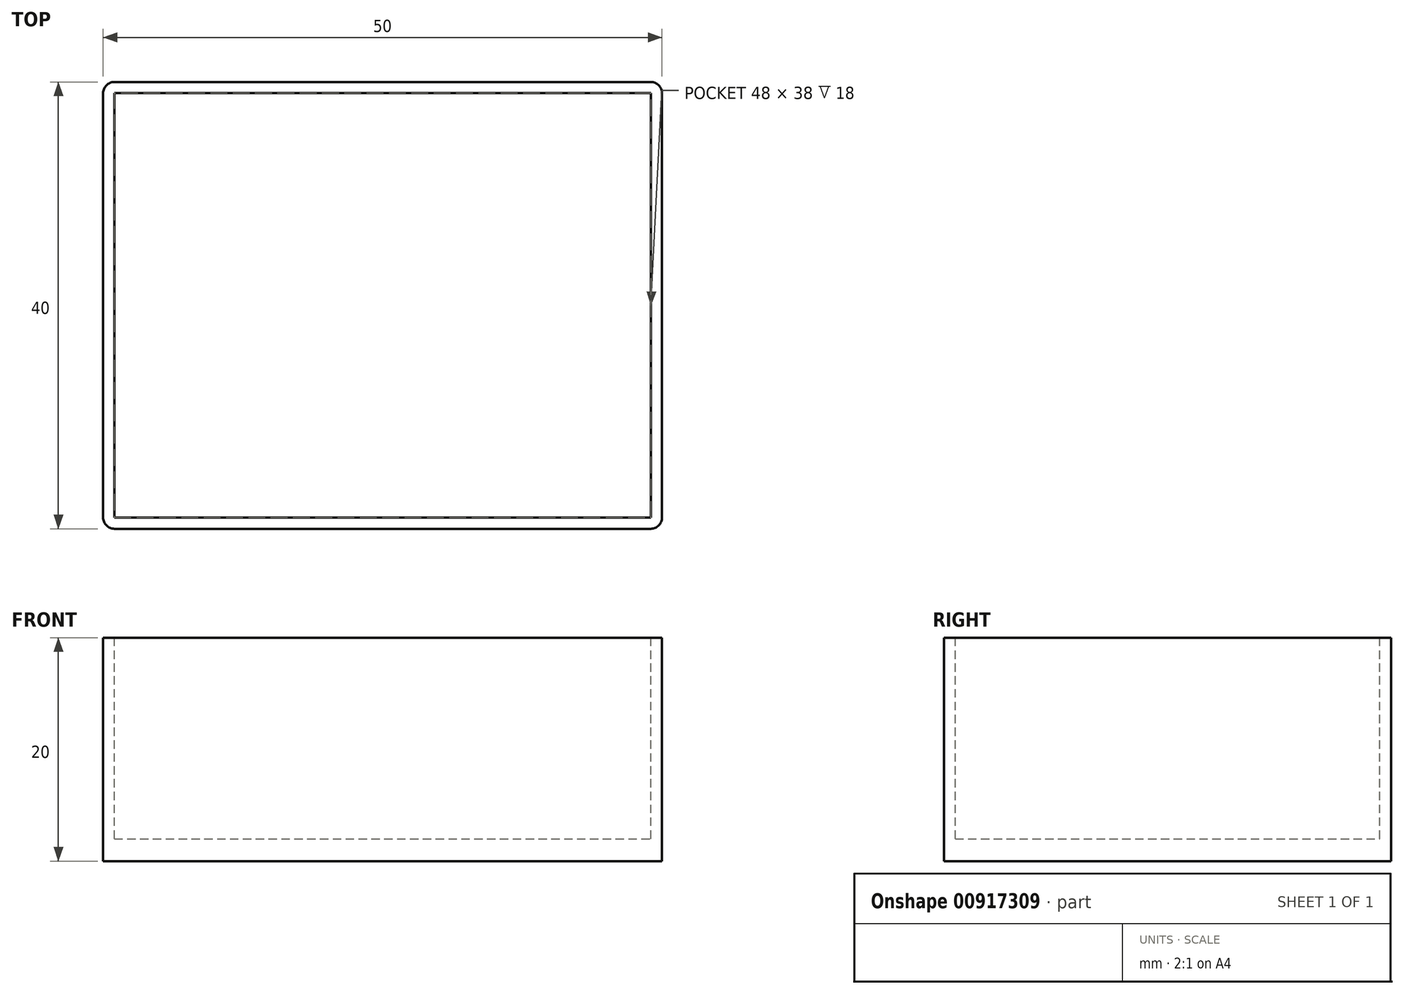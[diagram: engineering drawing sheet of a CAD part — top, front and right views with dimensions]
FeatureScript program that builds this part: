
annotation { "Feature Type Name" : "Feature", "Feature Type Description" : "" }
export const myFeature = defineFeature(function(context is Context, id is Id, definition is map)
    precondition{}
    {
        {
            var Q0;
            Q0=qCreatedBy(makeId("Top.planeOp"),FACE);
            var sketch = newSketch(context, id + "F0", { "sketchPlane" : qUnion([Q0])});
            skLineSegment(sketch, "E0.bottom", {"start": v(-25, 20) * mm, "end": v(25, 20) * mm});
            skLineSegment(sketch, "E0.top", {"start": v(-25, -20) * mm, "end": v(25, -20) * mm});
            skLineSegment(sketch, "E0.left", {"start": v(-25, 20) * mm, "end": v(-25, -20) * mm});
            skLineSegment(sketch, "E0.right", {"start": v(25, 20) * mm, "end": v(25, -20) * mm});
            skPoint(sketch, "E0.middle", {"position": v(0, 0) * mm});
            skSolve(sketch);
        }
        {
            var Q0;
            Q0=makeQuery(id+"F0.imprint","IMPRINT",FACE,{"disambiguationData":[TD([[makeQuery(id+"F0.imprint","IMPRINT",EDGE,{"derivedFrom":sQuery(id+"F0.wireOp",EDGE,"E0.bottom")}),-1.0]])]});
            extrude(context, id + "F1", {"entities" : qUnion([Q0]), "depth" : 20 * mm, "offsetDistance" : 25 * mm});
        }
        {
            var Q0;
            Q0=makeQuery(id+"F1.opExtrude","CAP_FACE",FACE,{"disambiguationData":[OSD([sQuery(id+"F0.wireOp",EDGE,"E0.bottom"),sQuery(id+"F0.wireOp",EDGE,"E0.top"),sQuery(id+"F0.wireOp",EDGE,"E0.left"),sQuery(id+"F0.wireOp",EDGE,"E0.right")])],"isStart":false});
            var sketch = newSketch(context, id + "F2", { "sketchPlane" : qUnion([Q0])});
            skLineSegment(sketch, "E1.bottom", {"start": v(-24, -19) * mm, "end": v(24, -19) * mm});
            skLineSegment(sketch, "E1.top", {"start": v(-24, 19) * mm, "end": v(24, 19) * mm});
            skLineSegment(sketch, "E1.left", {"start": v(-24, -19) * mm, "end": v(-24, 19) * mm});
            skLineSegment(sketch, "E1.right", {"start": v(24, -19) * mm, "end": v(24, 19) * mm});
            skPoint(sketch, "E1.middle", {"position": v(0, 0) * mm});
            skSolve(sketch);
        }
        {
            var Q0;
            Q0 = qSketchRegion(id + "F2", true);
            extrude(context, id + "F3", {"entities" : qUnion([Q0]), "operationType" : NewBodyOperationType.REMOVE, "oppositeDirection" : true, "depth" : 18 * mm, "offsetDistance" : 25 * mm});
        }
        {
            var Q0;
            Q0=makeQuery(id+"F1.opExtrude","SWEPT_EDGE",EDGE,{"disambiguationData":[OSD([sQuery(id+"F0.wireOp",EDGE,"E0.top"),sQuery(id+"F0.wireOp",EDGE,"E0.right")])]});
            var Q1;
            Q1=makeQuery(id+"F1.opExtrude","SWEPT_EDGE",EDGE,{"disambiguationData":[OSD([sQuery(id+"F0.wireOp",EDGE,"E0.bottom"),sQuery(id+"F0.wireOp",EDGE,"E0.right")])]});
            var Q2;
            Q2=makeQuery(id+"F1.opExtrude","SWEPT_EDGE",EDGE,{"disambiguationData":[OSD([sQuery(id+"F0.wireOp",EDGE,"E0.bottom"),sQuery(id+"F0.wireOp",EDGE,"E0.left")])]});
            var Q3;
            Q3=makeQuery(id+"F1.opExtrude","SWEPT_EDGE",EDGE,{"disambiguationData":[OSD([sQuery(id+"F0.wireOp",EDGE,"E0.top"),sQuery(id+"F0.wireOp",EDGE,"E0.left")])]});
            fillet(context, id + "F4", {"entities" : qUnion([Q0, Q1, Q2, Q3]), "radius" : 1 * mm, "tangentPropagation" : true, "allowEdgeOverflow" : false});
        }
    });
